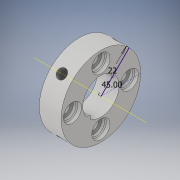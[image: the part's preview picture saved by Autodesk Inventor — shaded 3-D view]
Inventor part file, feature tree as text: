
AUTODESK INVENTOR PART (.ipt)
format: ipt  version: 2019 (Build 230136000, 136)  size: 207,360 bytes
history: native  units: in
note: dims shown in document units (in); Inventor stores cm internally (conversion verified against a paired STEP export)
features: sketch x6, extrude x5, plane x2, mirror x2, thread x1, chamfer x1, pattern_circular x1
ambient origin geometry x8: Origin, YZ Plane, XZ Plane, XY Plane, X Axis, Y Axis, Z Axis, Center Point
bodies: Solid1 (feature_tree)
feature tree (18):
  extrude  "Extrusion1"  Depth=1.7323in
  extrude  "Extrusion3"  Depth=1.2402in
  extrude  "Extrusion4"  Depth=1.1811in TaperAngle=0.0deg
  sketch  "Sketch6"  dims[d13=1.5748in d14=360.0deg d16=0.3937in d17=45.0deg]
  plane  "Work Plane1"
  extrude  "Extrusion5"  Depth=0.3937in
  plane  "Work Plane2"
  thread  "Thread1"  [1 undecoded]
  mirror  "Mirror1"
  extrude  "Extrusion6"  TaperAngle=45.0deg  [1 undecoded]
  chamfer  "Chamfer2"  Distance=0.1575in
  pattern_circular  "Circular Pattern1"  [2 undecoded]
  mirror  "Mirror2"
  sketch  "Sketch2"  dims[d3=0.7874in d4=1.7323in]
  sketch  "Sketch4"  dims[d5=0.4724in d6=0.0in d9=1.2402in]
  sketch  "Sketch5"  dims[d10=0.2008in d11=1.1811in d12=0.0in]
  sketch  "Sketch7"  dims[d18=0.1181in d19=45.0deg]
  sketch  "Sketch8"  dims[d20=0.3543in d21=0.1575in d22=0.0in d23=0.8661in d24=45.0deg d25=0.2047in d26=0.3937in d27=0.0in d28=0.3937in d29=0.0in d33=0.3937in d34=0.0787in d35=0.0in d36=0.0197in d37=0.0787in d38=0.2542in]
note: 4 required parameter values undecoded (feature->parameter linkage not recoverable at this tier; creation-order binding heuristic only, values carry confidence <= 0.55)
